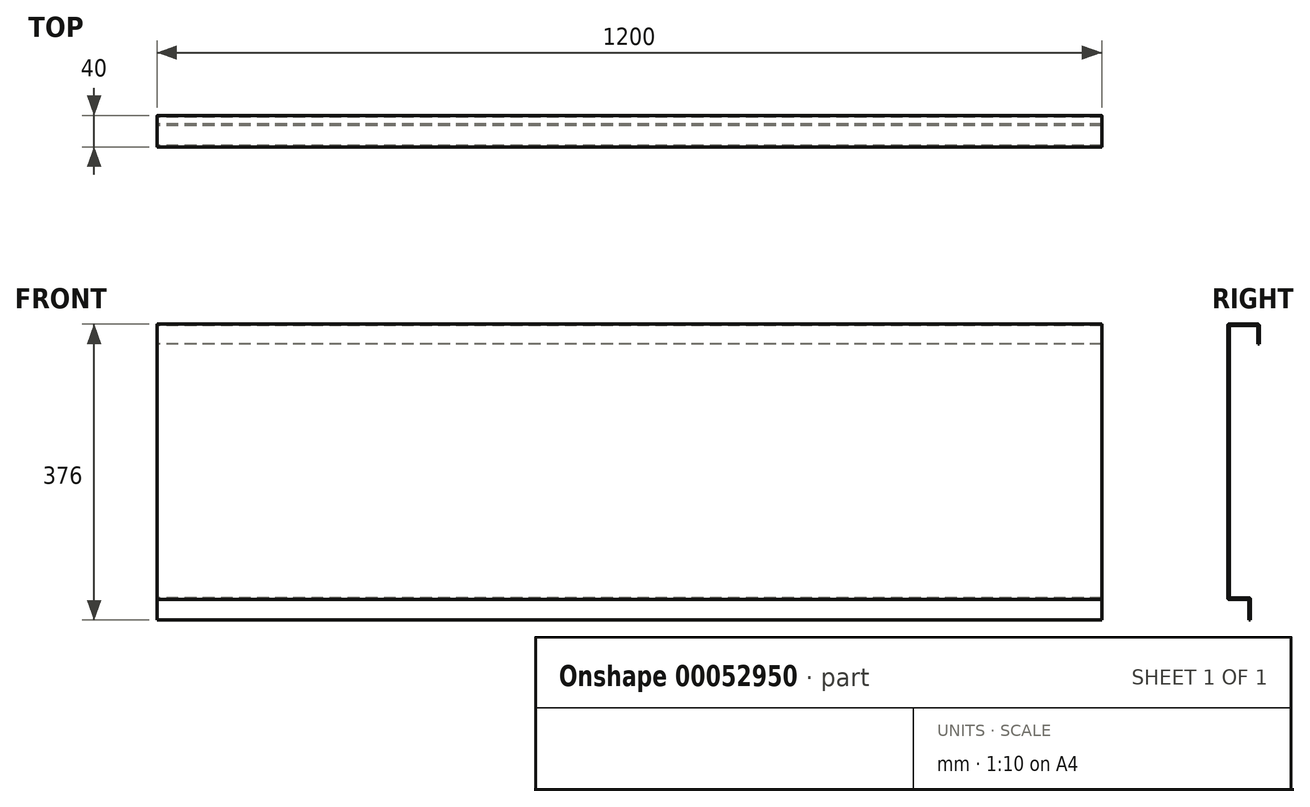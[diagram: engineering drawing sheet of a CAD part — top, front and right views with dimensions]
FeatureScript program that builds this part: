
annotation { "Feature Type Name" : "Feature", "Feature Type Description" : "" }
export const myFeature = defineFeature(function(context is Context, id is Id, definition is map)
    precondition{}
    {
        {
            var Q0;
            Q0=qCreatedBy(makeId("Right.planeOp"),FACE);
            var sketch = newSketch(context, id + "F0", { "sketchPlane" : qUnion([Q0])});
            skLineSegment(sketch, "E0", {"start": v(0, 0) * mm, "end": v(0, 430) * mm, "construction": true});
            skLineSegment(sketch, "E1", {"start": v(0, 0) * mm, "end": v(-250, 0) * mm, "construction": true});
            skLineSegment(sketch, "E2", {"start": v(-18.84, 404.8) * mm, "end": v(-18.84, 427.8) * mm});
            skLineSegment(sketch, "E3", {"start": v(-18.84, 427.8) * mm, "end": v(-54.84, 427.8) * mm});
            skLineSegment(sketch, "E4", {"start": v(-54.84, 427.8) * mm, "end": v(-54.84, 81.8) * mm});
            skLineSegment(sketch, "E5", {"start": v(-54.84, 81.8) * mm, "end": v(-27.84, 81.8) * mm});
            skLineSegment(sketch, "E6.0", {"start": v(-56.84, 79.8) * mm, "end": v(-29.84, 79.8) * mm});
            skLineSegment(sketch, "E6.1", {"start": v(-56.84, 429.8) * mm, "end": v(-56.84, 79.8) * mm});
            skLineSegment(sketch, "E6.2", {"start": v(-16.84, 429.8) * mm, "end": v(-56.84, 429.8) * mm});
            skLineSegment(sketch, "E6.3", {"start": v(-16.84, 404.8) * mm, "end": v(-16.84, 429.8) * mm});
            skLineSegment(sketch, "E7", {"start": v(-27.84, 81.8) * mm, "end": v(-27.84, 53.8) * mm});
            skLineSegment(sketch, "E8", {"start": v(-29.84, 79.8) * mm, "end": v(-29.84, 53.8) * mm});
            skLineSegment(sketch, "E9", {"start": v(-16.84, 404.8) * mm, "end": v(-18.84, 404.8) * mm});
            skLineSegment(sketch, "E10", {"start": v(-27.84, 53.8) * mm, "end": v(-29.84, 53.8) * mm});
            skSolve(sketch);
        }
        {
            var Q0;
            Q0=makeQuery(id+"F0.imprint","IMPRINT",FACE,{"disambiguationData":[TD([[makeQuery(id+"F0.imprint","IMPRINT",EDGE,{"derivedFrom":sQuery(id+"F0.wireOp",EDGE,"97aded3f-c788-494d-ab92-4e00cf807f6c")}),-1.0]])]});
            var Q1;
            Q1=makeQuery(id+"F0.imprint","IMPRINT",FACE,{"disambiguationData":[TD([[makeQuery(id+"F0.imprint","IMPRINT",EDGE,{"derivedFrom":sQuery(id+"F0.wireOp",EDGE,"E2")}),-1.0]])]});
            extrude(context, id + "F1", {"entities" : qUnion([Q0, Q1]), "depth" : 1200 * mm});
        }
        {
            var Q0;
            Q0=makeQuery(id+"F1.opExtrude","SWEPT_EDGE",EDGE,{"disambiguationData":[OSD([sQuery(id+"F0.wireOp",EDGE,"E6.1"),sQuery(id+"F0.wireOp",EDGE,"E6.2")])]});
            var Q1;
            Q1=makeQuery(id+"F1.opExtrude","SWEPT_EDGE",EDGE,{"disambiguationData":[OSD([sQuery(id+"F0.wireOp",EDGE,"E6.2"),sQuery(id+"F0.wireOp",EDGE,"E6.3")])]});
            var Q2;
            Q2=makeQuery(id+"F1.opExtrude","SWEPT_EDGE",EDGE,{"disambiguationData":[OSD([sQuery(id+"F0.wireOp",EDGE,"E6.0"),sQuery(id+"F0.wireOp",EDGE,"E6.1")])]});
            var Q3;
            Q3=makeQuery(id+"F1.opExtrude","SWEPT_EDGE",EDGE,{"disambiguationData":[OSD([sQuery(id+"F0.wireOp",EDGE,"E5"),sQuery(id+"F0.wireOp",EDGE,"E7")])]});
            var Q4;
            Q4=makeQuery(id+"F1.opExtrude","SWEPT_EDGE",EDGE,{"disambiguationData":[OSD([sQuery(id+"F0.wireOp",EDGE,"E4"),sQuery(id+"F0.wireOp",EDGE,"E5")])]});
            var Q5;
            Q5=makeQuery(id+"F1.opExtrude","SWEPT_EDGE",EDGE,{"disambiguationData":[OSD([sQuery(id+"F0.wireOp",EDGE,"E6.0"),sQuery(id+"F0.wireOp",EDGE,"E8")])]});
            var Q6;
            Q6=makeQuery(id+"F1.opExtrude","SWEPT_EDGE",EDGE,{"disambiguationData":[OSD([sQuery(id+"F0.wireOp",EDGE,"E2"),sQuery(id+"F0.wireOp",EDGE,"E3")])]});
            var Q7;
            Q7=makeQuery(id+"F1.opExtrude","SWEPT_EDGE",EDGE,{"disambiguationData":[OSD([sQuery(id+"F0.wireOp",EDGE,"E3"),sQuery(id+"F0.wireOp",EDGE,"E4")])]});
            fillet(context, id + "F2", {"entities" : qUnion([Q0, Q1, Q2, Q3, Q4, Q5, Q6, Q7]), "radius" : 2 * mm, "tangentPropagation" : true, "allowEdgeOverflow" : false});
        }
    });
